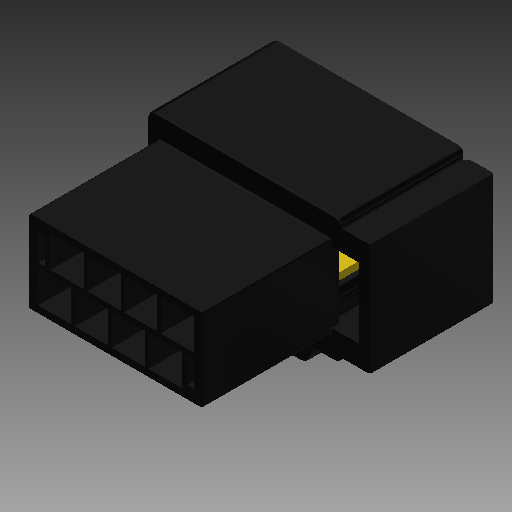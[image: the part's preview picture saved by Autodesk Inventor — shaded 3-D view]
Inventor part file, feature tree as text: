
AUTODESK INVENTOR PART (.ipt)
format: ipt  version: 2019 (Build 230136000, 136)  size: 805,888 bytes
history: native  units: mm
features: extrude x12, sketch x12, fillet x7, chamfer x3, pattern_linear x2
ambient origin geometry x8: Origin, YZ Plane, XZ Plane, XY Plane, X Axis, Y Axis, Z Axis, Center Point
bodies: Solid1 (feature_tree), Solid2 (feature_tree)
feature tree (36):
  extrude  "Extrusion1"  Depth=11.938mm
  extrude  "Extrusion2"  Depth=1.778mm
  extrude  "Extrusion3"  Depth=1.016mm
  extrude  "Extrusion4"  Depth=1.016mm
  extrude  "Extrusion5"  Depth=4.572mm
  extrude  "Extrusion6"  Depth=4.826mm
  fillet  "Fillet1"  Radius=0.508mm
  fillet  "Fillet2"  Radius=4.826mm
  fillet  "Fillet3"  Radius=0.508mm
  chamfer  "Chamfer1"  Distance=0.762mm
  extrude  "Extrusion7"  Depth=0.254mm
  pattern_linear  "Rectangular Pattern1"  Spacing1=0.508mm  [1 undecoded]
  extrude  "Extrusion8"  Depth=0.254mm
  pattern_linear  "Rectangular Pattern2"  Spacing1=0.508mm  [1 undecoded]
  extrude  "Extrusion9"  Depth=0.254mm
  extrude  "Extrusion10"  Depth=0.254mm
  extrude  "Extrusion11"  Depth=0.254mm
  chamfer  "Chamfer2"  Distance=18.669mm
  chamfer  "Chamfer3"  Distance=1.626mm
  fillet  "Fillet5"  Radius=3.048mm
  fillet  "Fillet6"  Radius=28.397mm
  extrude  "Extrusion12"  Depth=0.254mm
  fillet  "Fillet7"  Radius=0.991mm
  fillet  "Fillet8"  Radius=16.256mm
  sketch  "Sketch1"  dims[d0=25.146mm d1=11.938mm]
  sketch  "Sketch2"  dims[d2=1.27mm d3=1.778mm]
  sketch  "Sketch3"  dims[d4=3.81mm d5=1.016mm]
  sketch  "Sketch4"  dims[d6=0.762mm d7=1.016mm]
  sketch  "Sketch5"  dims[d8=4.826mm d9=4.572mm]
  sketch  "Sketch6"  dims[d11=0.508mm d12=4.826mm d13=0.508mm d14=4.826mm d15=0.508mm]
  sketch  "Sketch7"  dims[d16=4.826mm]
  sketch  "Sketch8"  dims[d17=1.78mm]
  sketch  "Sketch9"  dims[d18=1.016mm]
  sketch  "Sketch10"  dims[d19=1.016mm]
  sketch  "Sketch12"  dims[d20=1.27mm]
  sketch  "Sketch13"  dims[d21=3.81mm d22=0.762mm d23=4.826mm d24=0.508mm d25=4.826mm d26=0.508mm d27=4.826mm d28=0.508mm d29=4.826mm d30=18.669mm d31=0.0mm d47=1.626mm d48=3.048mm d49=28.397mm d50=3.937mm d51=0.991mm d52=16.256mm d53=18.034mm d54=2.591mm d55=4.597mm d56=6.604mm d57=6.604mm d58=5.994mm d59=4.534mm d60=3.028mm d61=10.2mm d62=1.499mm d63=1.168mm d64=0.0mm d65=1.499mm d66=1.499mm d67=1.499mm d68=1.499mm d69=1.499mm d70=1.499mm d71=1.499mm d72=1.499mm d73=1.499mm d74=1.626mm d75=1.499mm d76=1.499mm d77=1.499mm d78=1.626mm d79=1.499mm d80=16.815mm d81=0.0mm d82=7.353mm d83=1.651mm d84=1.27mm d85=11.659mm d86=1.27mm d87=2.54mm d88=1.27mm d89=3.035mm d90=1.27mm d91=12.37mm d92=0.0mm d93=17.628mm d94=1.016mm d95=4.064mm d96=5.842mm d97=1.524mm d98=0.0mm d99=7.01mm d100=2.591mm d101=0.0mm d102=1.778mm d103=1.753mm d104=0.279mm d105=0.254mm d106=0.254mm d107=1.27mm d108=0.254mm d109=2.54mm d110=3.0mm d111=2.0mm d112=4.63734mm d113=0.702mm d114=0.594mm d115=1.0mm d116=1.896mm d117=0.812mm d118=1.004mm d119=1.193mm d120=1.004mm d121=1.406mm d122=2.014mm d123=2.591mm d124=0.0mm d125=40.0mm d127=5.334mm d128=0.702mm d129=0.594mm d130=1.0mm d131=1.896mm d132=0.812mm d133=1.004mm d134=1.193mm d135=1.004mm d136=1.406mm d137=2.014mm d138=2.591mm d139=0.0mm d140=40.0mm d142=5.334mm d143=1.27mm d144=1.397mm d145=2.286mm d146=0.5mm d147=1.016mm d148=1.409mm d149=0.761mm d150=1.016mm d151=1.409mm d152=0.5mm d153=1.168mm d154=0.0mm d155=0.737mm d156=1.381mm d157=1.381mm d158=0.737mm d159=1.168mm d160=0.0mm d161=10.332mm d162=0.0mm d163=0.7mm d164=2.0mm d165=0.174533mm d166=0.3mm d167=2.0mm d168=0.174533mm d170=1.27mm d171=0.254mm d174=1.168mm d175=0.0mm d176=0.9mm d177=0.254mm]
note: 2 required parameter values undecoded (feature->parameter linkage not recoverable at this tier; creation-order binding heuristic only, values carry confidence <= 0.55)
